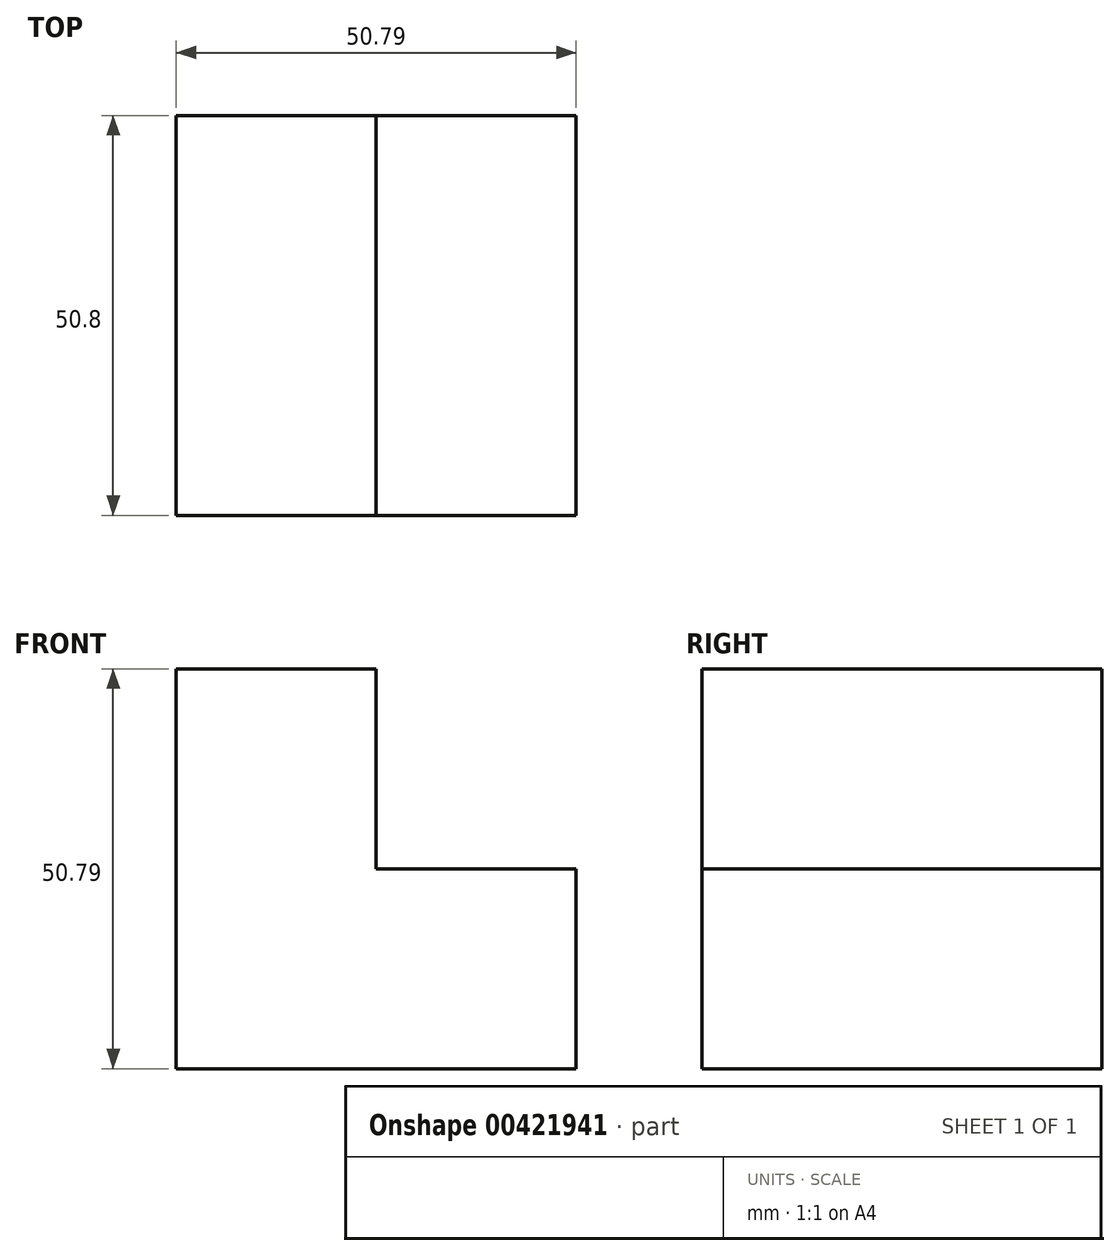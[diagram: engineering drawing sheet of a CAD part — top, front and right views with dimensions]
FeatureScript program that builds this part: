
annotation { "Feature Type Name" : "Feature", "Feature Type Description" : "" }
export const myFeature = defineFeature(function(context is Context, id is Id, definition is map)
    precondition{}
    {
        {
            var Q0;
            Q0=qCreatedBy(makeId("Front.planeOp"),FACE);
            var sketch = newSketch(context, id + "F0", { "sketchPlane" : qUnion([Q0])});
            skLineSegment(sketch, "E0", {"start": v(0, 0) * mm, "end": v(-50.8, 0) * mm});
            skLineSegment(sketch, "E1", {"start": v(-50.8, 0) * mm, "end": v(-50.8, 50.8) * mm});
            skLineSegment(sketch, "E2", {"start": v(0, 0) * mm, "end": v(0, 25.4) * mm});
            skLineSegment(sketch, "E3", {"start": v(0, 25.4) * mm, "end": v(-25.4, 25.4) * mm});
            skLineSegment(sketch, "E4", {"start": v(-25.4, 25.4) * mm, "end": v(-25.4, 50.8) * mm});
            skLineSegment(sketch, "E5", {"start": v(-50.8, 50.8) * mm, "end": v(-25.4, 50.8) * mm});
            skSolve(sketch);
        }
        {
            var Q0;
            Q0 = qSketchRegion(id + "F0", true);
            extrude(context, id + "F1", {"entities" : qUnion([Q0]), "depth" : 50.8 * mm});
        }
    });
